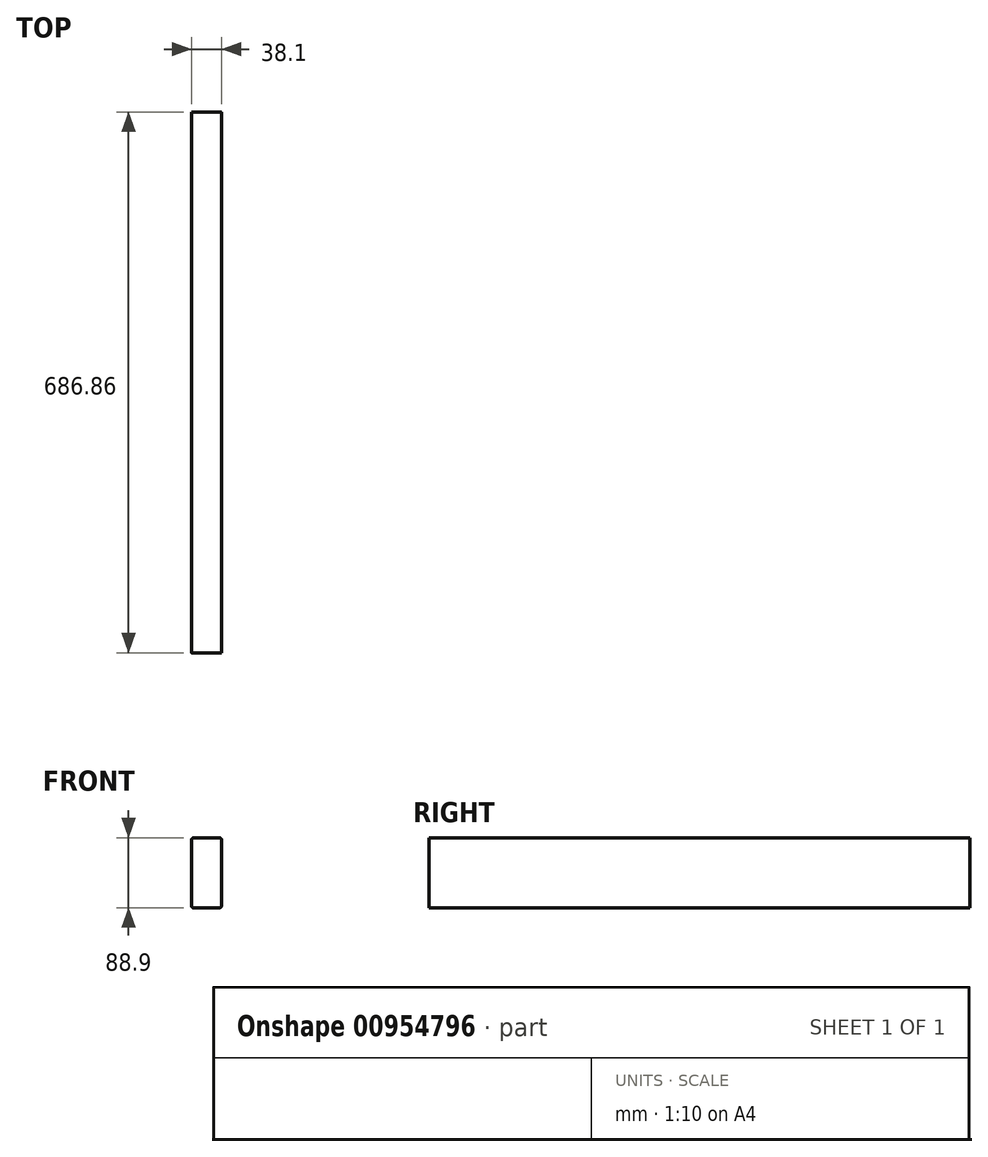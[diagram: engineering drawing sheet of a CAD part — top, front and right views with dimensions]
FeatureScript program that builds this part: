
annotation { "Feature Type Name" : "Feature", "Feature Type Description" : "" }
export const myFeature = defineFeature(function(context is Context, id is Id, definition is map)
    precondition{}
    {
        {
            var Q0;
            Q0=qCreatedBy(makeId("Front.planeOp"),FACE);
            var sketch = newSketch(context, id + "F0", { "sketchPlane" : qUnion([Q0])});
            skLineSegment(sketch, "E0.bottom", {"start": v(19.05, 44.45) * mm, "end": v(-19.05, 44.45) * mm});
            skLineSegment(sketch, "E0.top", {"start": v(19.05, -44.45) * mm, "end": v(-19.05, -44.45) * mm});
            skLineSegment(sketch, "E0.left", {"start": v(19.05, 44.45) * mm, "end": v(19.05, -44.45) * mm});
            skLineSegment(sketch, "E0.right", {"start": v(-19.05, 44.45) * mm, "end": v(-19.05, -44.45) * mm});
            skPoint(sketch, "E0.middle", {"position": v(0, 0) * mm});
            skSolve(sketch);
        }
        {
            var Q0;
            Q0 = qSketchRegion(id + "F0", true);
            extrude(context, id + "F1", {"entities" : qUnion([Q0]), "depth" : 54 / 50.8 * mm, "offsetDistance" : 25.4 * mm, "hasSecondDirection" : true, "secondDirectionOppositeDirection" : true, "secondDirectionDepth" : 685.8 * mm});
        }
        {
            var Q0;
            Q0=makeQuery(id+"F1.opExtrude","SWEPT_FACE",FACE,{"disambiguationData":[OSD([sQuery(id+"F0.wireOp",EDGE,"E0.left")])]});
            var sketch = newSketch(context, id + "F2", { "sketchPlane" : qUnion([Q0])});
            skCircle(sketch, "E1", {"center": v(-666.75, 22.22) * mm, "radius": 3.18 * mm});
            skLineSegment(sketch, "E2.bottom", {"start": v(-685.8, 44.45) * mm, "end": v(-647.7, 44.45) * mm, "construction": true});
            skLineSegment(sketch, "E2.top", {"start": v(-685.8, -44.45) * mm, "end": v(-647.7, -44.45) * mm, "construction": true});
            skLineSegment(sketch, "E2.left", {"start": v(-685.8, 44.45) * mm, "end": v(-685.8, -44.45) * mm, "construction": true});
            skLineSegment(sketch, "E2.right", {"start": v(-647.7, 44.45) * mm, "end": v(-647.7, -44.45) * mm, "construction": true});
            skLineSegment(sketch, "E3", {"start": v(-685.8, 22.22) * mm, "end": v(-647.7, 22.22) * mm, "construction": true});
            skSolve(sketch);
        }
        {
            var Q0;
            Q0 = qSketchRegion(id + "F2", true);
            extrude(context, id + "F3", {"entities" : qUnion([Q0]), "operationType" : NewBodyOperationType.REMOVE, "oppositeDirection" : true, "depth" : 12.7 * mm, "offsetDistance" : 25.4 * mm});
        }
        {
            var Q0;
            Q0=makeQuery(id+"F1.opExtrude","SWEPT_EDGE",EDGE,{"disambiguationData":[OSD([sQuery(id+"F0.wireOp",EDGE,"E0.bottom"),sQuery(id+"F0.wireOp",EDGE,"E0.left")])]});
            var Q1;
            Q1=makeQuery(id+"F1.opExtrude","SWEPT_EDGE",EDGE,{"disambiguationData":[OSD([sQuery(id+"F0.wireOp",EDGE,"E0.bottom"),sQuery(id+"F0.wireOp",EDGE,"E0.right")])]});
            var Q2;
            Q2=makeQuery(id+"F1.opExtrude","SWEPT_EDGE",EDGE,{"disambiguationData":[OSD([sQuery(id+"F0.wireOp",EDGE,"E0.top"),sQuery(id+"F0.wireOp",EDGE,"E0.left")])]});
            var Q3;
            Q3=makeQuery(id+"F1.opExtrude","SWEPT_EDGE",EDGE,{"disambiguationData":[OSD([sQuery(id+"F0.wireOp",EDGE,"E0.top"),sQuery(id+"F0.wireOp",EDGE,"E0.right")])]});
            fillet(context, id + "F4", {"entities" : qUnion([Q0, Q1, Q2, Q3]), "radius" : 2.54 * mm, "tangentPropagation" : true, "allowEdgeOverflow" : false});
        }
    });
